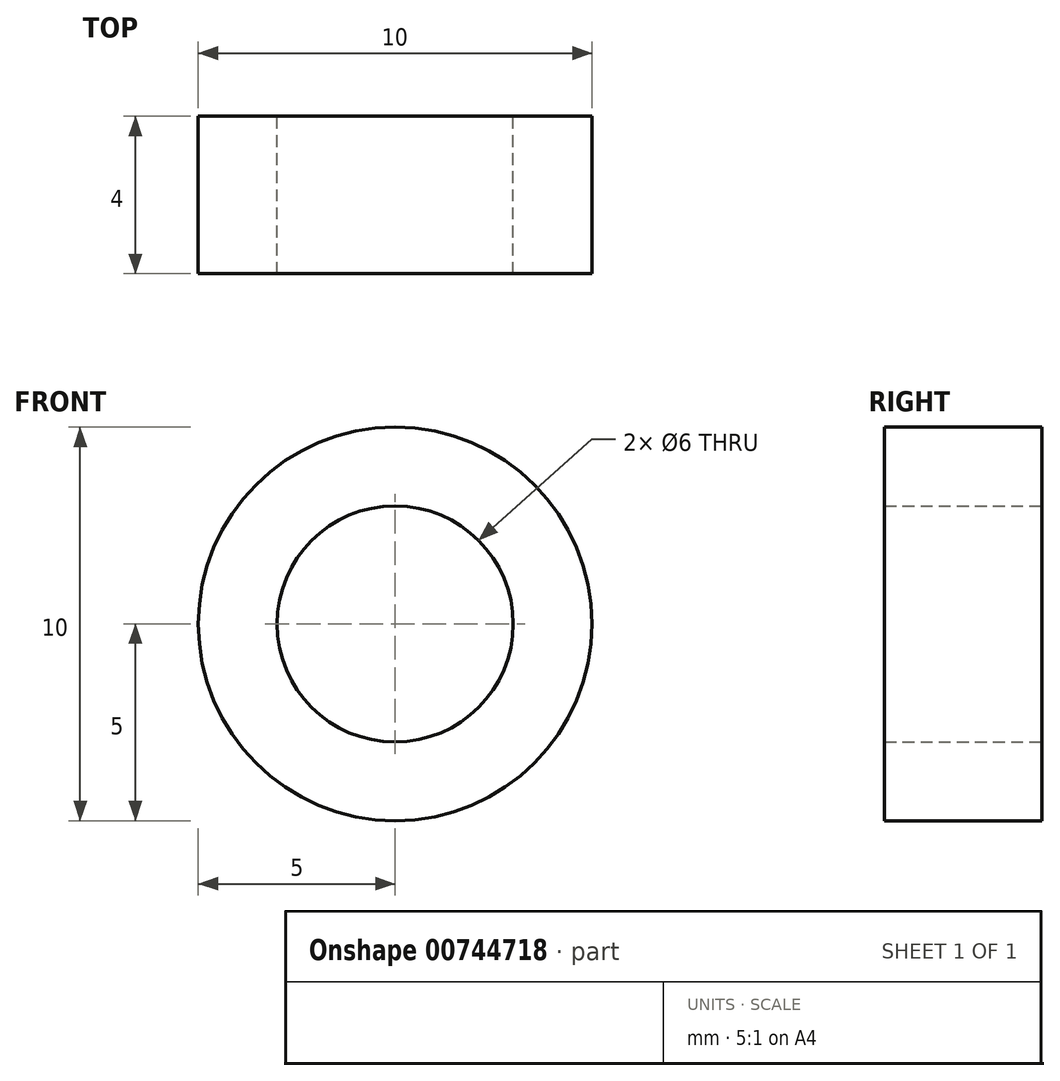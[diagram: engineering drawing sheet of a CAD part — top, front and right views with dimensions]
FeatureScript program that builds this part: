
annotation { "Feature Type Name" : "Feature", "Feature Type Description" : "" }
export const myFeature = defineFeature(function(context is Context, id is Id, definition is map)
    precondition{}
    {
        {
            var Q0;
            Q0=qCreatedBy(makeId("Front.planeOp"),FACE);
            var sketch = newSketch(context, id + "F0", { "sketchPlane" : qUnion([Q0])});
            skCircle(sketch, "E0", {"center": v(0, 0) * mm, "radius": 3 * mm});
            skCircle(sketch, "E1", {"center": v(0, 0) * mm, "radius": 5 * mm});
            skSolve(sketch);
        }
        {
            var Q0;
            Q0 = qSketchRegion(id + "F0", true);
            extrude(context, id + "F1", {"entities" : qUnion([Q0]), "depth" : 4 * mm, "offsetDistance" : 25 * mm});
        }
    });
